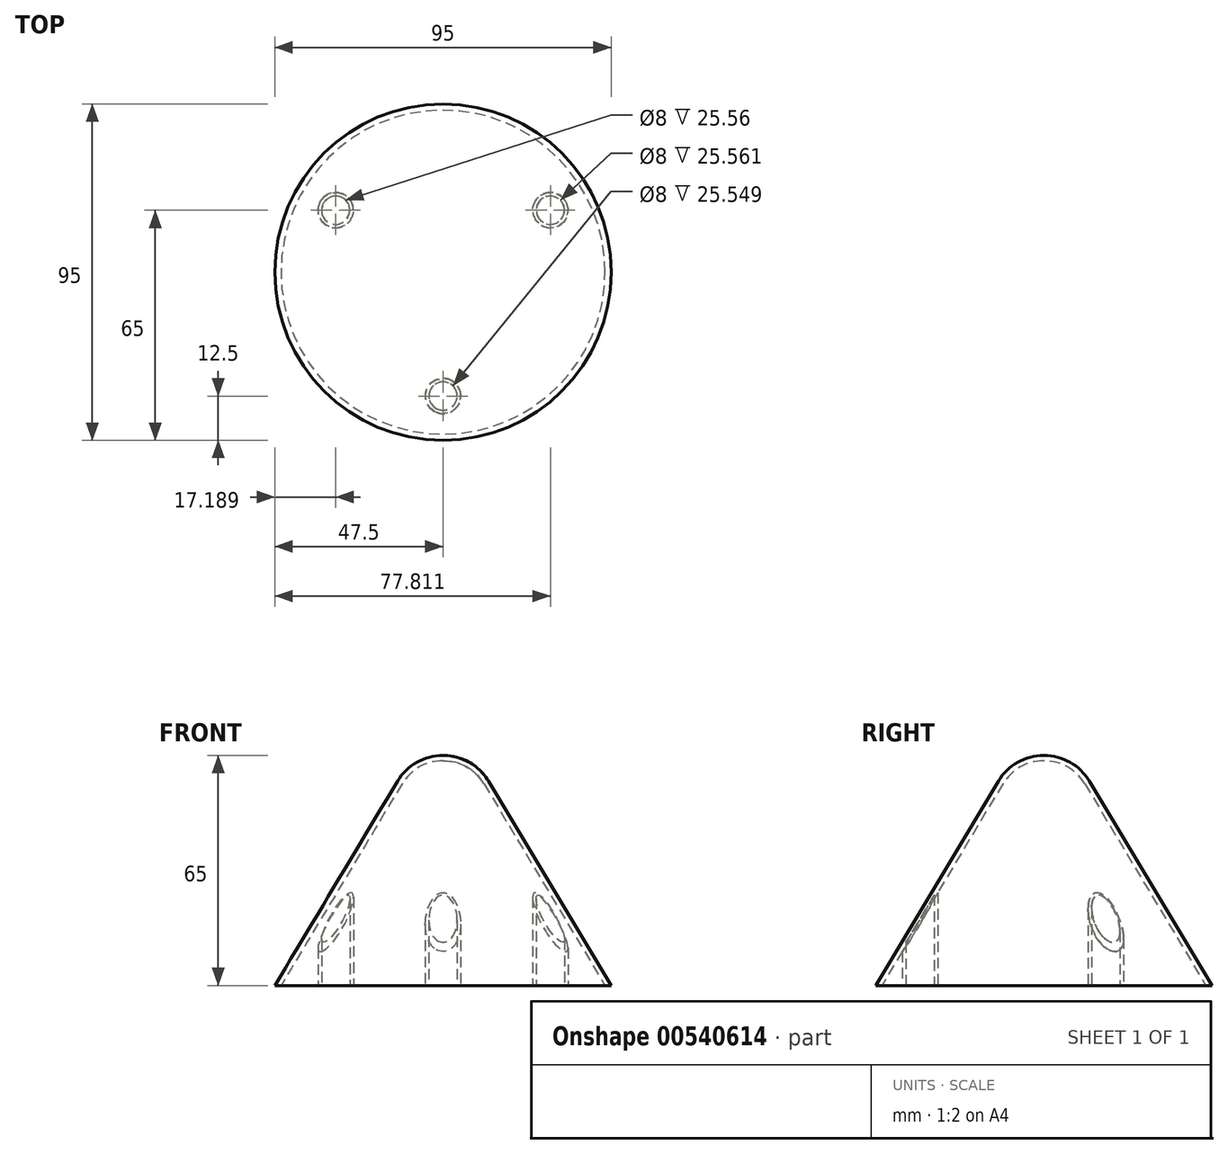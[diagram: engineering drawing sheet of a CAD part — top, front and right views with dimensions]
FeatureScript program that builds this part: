
annotation { "Feature Type Name" : "Feature", "Feature Type Description" : "" }
export const myFeature = defineFeature(function(context is Context, id is Id, definition is map)
    precondition{}
    {
        {
            var Q0;
            Q0=qCreatedBy(makeId("Front.planeOp"),FACE);
            var sketch = newSketch(context, id + "F0", { "sketchPlane" : qUnion([Q0])});
            skLineSegment(sketch, "E0", {"start": v(0, 0) * mm, "end": v(47.5, 0) * mm});
            skLineSegment(sketch, "E1", {"start": v(0, 0) * mm, "end": v(0, 50) * mm});
            skArc(sketch, "E2", {"start": v(12.86, 57.72) * mm, "mid": v(7.39, 63.05) * mm, "end": v(0, 65) * mm});
            skLineSegment(sketch, "E3", {"start": v(12.86, 57.72) * mm, "end": v(47.5, 0) * mm});
            skLineSegment(sketch, "E4", {"start": v(0, 50) * mm, "end": v(0, 65) * mm});
            skPoint(sketch, "E5.orphan", {"position": v(-12.86, 57.72) * mm});
            skSolve(sketch);
        }
        {
            var Q0;
            Q0=makeQuery(id+"F0.imprint","IMPRINT",FACE,{"disambiguationData":[TD([[makeQuery(id+"F0.imprint","IMPRINT",EDGE,{"derivedFrom":sQuery(id+"F0.wireOp",EDGE,"E0")}),1.0]])]});
            var Q1;
            Q1=sQuery(id+"F0.wireOp",EDGE,"E1");
            revolve(context, id + "F1", {"entities" : qUnion([Q0]), "axis" : qUnion([Q1]), "revolveType" : RevolveType.FULL});
        }
        {
            var Q0;
            Q0=makeQuery(id+"F1.opRevolve","SWEPT_FACE",FACE,{"disambiguationData":[OSD([sQuery(id+"F0.wireOp",EDGE,"E0")])]});
            shell(context, id + "F2", {"entities" : qUnion([Q0]), "thickness" : 1.5 * mm});
        }
        {
            var Q0;
            Q0=qCreatedBy(makeId("Top.planeOp"),FACE);
            var sketch = newSketch(context, id + "F3", { "sketchPlane" : qUnion([Q0])});
            skCircle(sketch, "E6", {"center": v(0, -35) * mm, "radius": 5 * mm});
            skCircle(sketch, "E7.1.0", {"center": v(30.31, 17.5) * mm, "radius": 5 * mm});
            skCircle(sketch, "E7.2.0", {"center": v(-30.31, 17.5) * mm, "radius": 5 * mm});
            skPoint(sketch, "E7.center", {"position": v(0, 0) * mm});
            skSolve(sketch);
        }
        {
            var Q0;
            Q0 = qSketchRegion(id + "F3", true);
            extrude(context, id + "F4", {"entities" : qUnion([Q0]), "operationType" : NewBodyOperationType.ADD, "endBound" : BoundingType.UP_TO_NEXT, "depth" : 25 * mm, "offsetDistance" : 25 * mm});
        }
        {
            var Q0;
            Q0=makeQuery(id+"F4.opExtrude","CAP_FACE",FACE,{"disambiguationData":[OSD([sQuery(id+"F3.wireOp",EDGE,"E7.1.0")])],"isStart":true});
            var Q1;
            Q1=makeQuery(id+"F4.opExtrude","CAP_FACE",FACE,{"disambiguationData":[OSD([sQuery(id+"F3.wireOp",EDGE,"E7.2.0")])],"isStart":true});
            var Q2;
            Q2=makeQuery(id+"F4.opExtrude","CAP_FACE",FACE,{"disambiguationData":[OSD([sQuery(id+"F3.wireOp",EDGE,"E6")])],"isStart":true});
            shell(context, id + "F5", {"entities" : qUnion([Q0, Q1, Q2]), "thickness" : 1 * mm});
        }
    });
